# Revit family: Lunar-Single_Glazed_Panels
name_source: partatom
category: Curtain Panels
revit_build: Autodesk Revit Architecture 2015 (Build: 20140606_1530(x64)
units: mm (PartAtom-declared; Revit-internal decimal feet)

## types (5) — shared parameters
Analytic Construction = <None>
BIMobject category = Curtain Walls
BIMobject category code = walls-curtain
BIMobject main category = Walls
BIMobject main category code = walls
Brand url = http://www.avantisystemsusa.com
Description = The system utilizes PDLC technology which allows completely transparent glass to transform to private in 1 milisecond.
Design country = United States
Edition number = 1
Glass Marker = Yes
Glazing Material = Glass - Avanti - Lunar™ Smart Glass Partition System
Inset = 0' - 0"
Manufacturer = Avanti Systems USA
Manufacturer name = Avanti Systems
Masterformat 2014 Code = 10 22 19
Masterformat 2014 Description = Demountable Partitions
Material main = Glass
Material secondary = Aluminium
Maximum Height = 12' - 0"
Maximum Width = 5' - 0"
Nominal height = 0' - 0"
Nominal width = 0' - 0"
Offset = 0' - 0 1/32"
OmniClass Code = 23-15 11 13
OmniClass Description = Demountable Partitions
Product Guid = 85a3f31c-26a6-4c7e-983f-18423418bcc4
Product SKU = avanti-lunar-lcd-privacy-smart-glass
Product data url = https://bimobject.com
Product family = Partition Systems
Product group = LCD Privacy Smart Glass
Product url = https://www.avantisystemsusa.com
QR code = http://bimobject.com
URL = https://www.avantisystemsusa.com
Uniclass 1.4 Code = L384
Uniclass 1.4 Description = Partitions, non-structural internal walls
Uniclass 2.0 Code = SS-25-10-30
Uniclass 2.0 Description = Framed Partition Systems
Uniclass 2015 Code = Ss_25_10_30
Uniclass 2015 Name = Framed partition systems
Uniformat II Code = C1010
Uniformat II Description = Partitions
Weight Net (Kg) = 0

## per-type parameters (varying)
| type | Thickness |
| Lunar™ LCD Privacy Smart Glass - Single Glazed 1/2" Panel | 0' - 0 1/2" |
| Lunar™ LCD Privacy Smart Glass - Single Glazed 3/4" Panel | 0' - 0 3/4" |
| Lunar™ LCD Privacy Smart Glass - Single Glazed 3/8" Panel | 0' - 0 3/8" |
| Lunar™ LCD Privacy Smart Glass - Single Glazed 7/16" Panel | 0' - 0 7/16" |
| Lunar™ LCD Privacy Smart Glass - Single Glazed 9/16" Panel | 0' - 0 9/16" |

note: column(s) folded — value = type name in every type: Model
